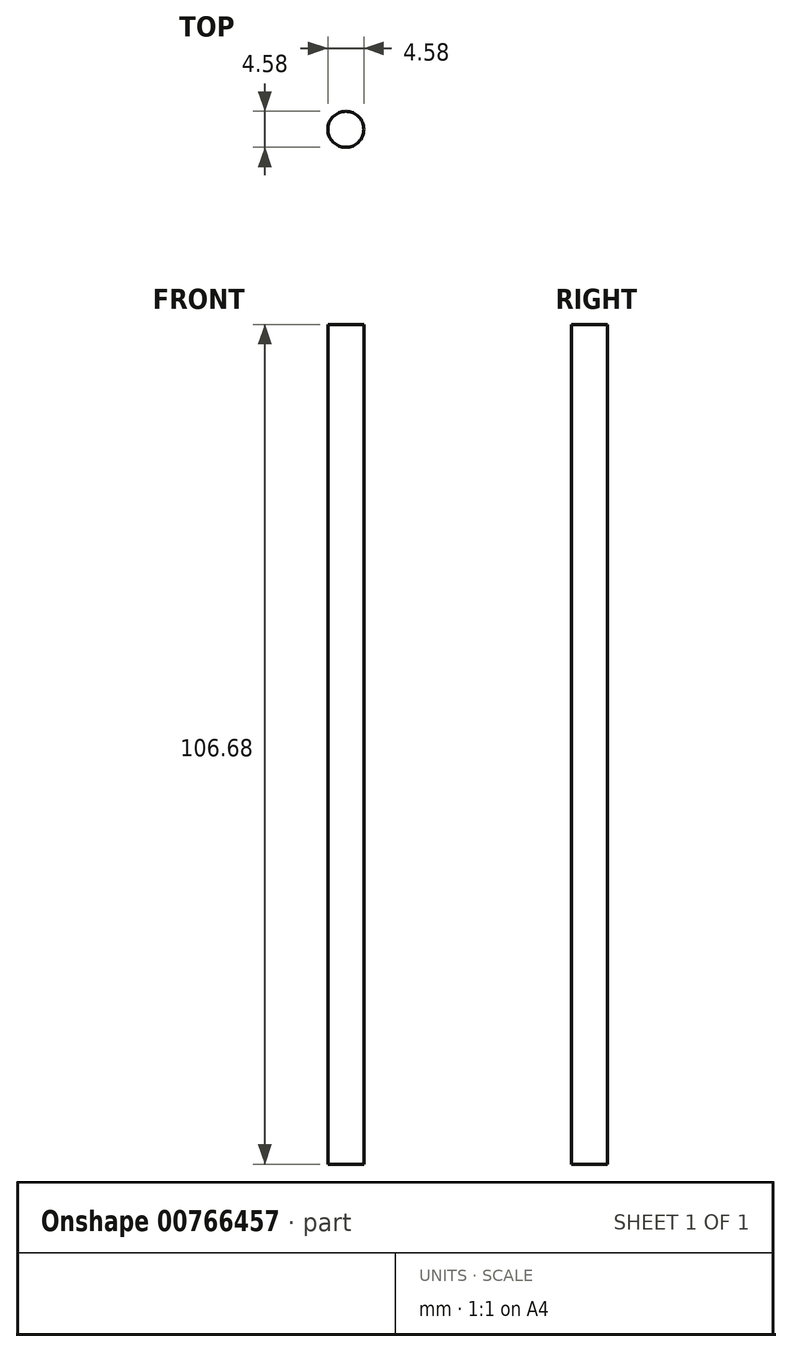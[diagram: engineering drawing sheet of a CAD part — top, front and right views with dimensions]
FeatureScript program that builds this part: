
annotation { "Feature Type Name" : "Feature", "Feature Type Description" : "" }
export const myFeature = defineFeature(function(context is Context, id is Id, definition is map)
    precondition{}
    {
        {
            var Q0;
            Q0=qCreatedBy(makeId("Top.planeOp"),FACE);
            var sketch = newSketch(context, id + "F0", { "sketchPlane" : qUnion([Q0])});
            skCircle(sketch, "E0", {"center": v(0, 0) * mm, "radius": 2.29 * mm});
            skSolve(sketch);
        }
        {
            var Q0;
            Q0=makeQuery(id+"F0.imprint","IMPRINT",FACE,{"disambiguationData":[TD([[makeQuery(id+"F0.imprint","IMPRINT",EDGE,{"derivedFrom":sQuery(id+"F0.wireOp",EDGE,"E0")}),1.0]])]});
            extrude(context, id + "F1", {"entities" : qUnion([Q0]), "depth" : 106.68 * mm, "offsetDistance" : 25.4 * mm});
        }
    });
